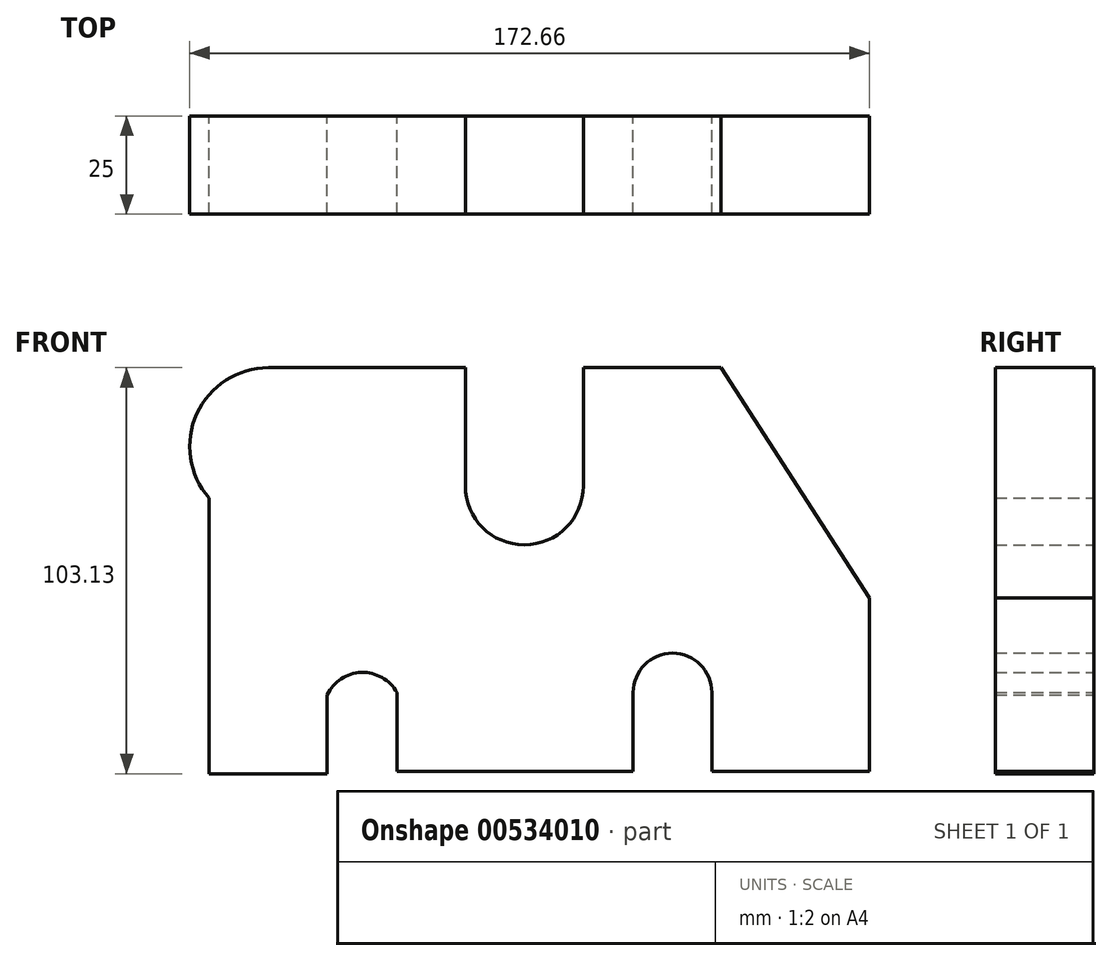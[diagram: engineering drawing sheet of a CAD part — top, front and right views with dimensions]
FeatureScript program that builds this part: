
annotation { "Feature Type Name" : "Feature", "Feature Type Description" : "" }
export const myFeature = defineFeature(function(context is Context, id is Id, definition is map)
    precondition{}
    {
        {
            var Q0;
            Q0=qCreatedBy(makeId("Front.planeOp"),FACE);
            var sketch = newSketch(context, id + "F0", { "sketchPlane" : qUnion([Q0])});
            skLineSegment(sketch, "E0", {"start": v(-105.28, 82.52) * mm, "end": v(-55.28, 82.52) * mm});
            skLineSegment(sketch, "E1", {"start": v(-55.28, 82.52) * mm, "end": v(-55.28, 52.52) * mm});
            skLineSegment(sketch, "E2", {"start": v(-25.28, 82.52) * mm, "end": v(-25.28, 52.52) * mm});
            skLineSegment(sketch, "E3", {"start": v(-25.28, 82.52) * mm, "end": v(9.72, 82.52) * mm});
            skLineSegment(sketch, "E4", {"start": v(9.72, 82.52) * mm, "end": v(47.38, 24) * mm});
            skLineSegment(sketch, "E5", {"start": v(38.76, -30.8) * mm, "end": v(37.94, -30.8) * mm});
            skLineSegment(sketch, "E6", {"start": v(-120.37, 49.39) * mm, "end": v(-120.37, -20.61) * mm});
            skLineSegment(sketch, "E7", {"start": v(-120.37, -20.61) * mm, "end": v(-90.37, -20.61) * mm});
            skArc(sketch, "E8", {"start": v(-55.28, 52.52) * mm, "mid": v(-40.28, 37.52) * mm, "end": v(-25.28, 52.52) * mm});
            skLineSegment(sketch, "E9", {"start": v(-72.62, -20) * mm, "end": v(-12.62, -20) * mm});
            skLineSegment(sketch, "E10", {"start": v(-12.62, -20) * mm, "end": v(-12.62, 0) * mm});
            skLineSegment(sketch, "E11", {"start": v(7.38, -20) * mm, "end": v(7.38, 0) * mm});
            skLineSegment(sketch, "E12", {"start": v(7.38, -20) * mm, "end": v(47.38, -20) * mm});
            skLineSegment(sketch, "E13", {"start": v(47.38, 24) * mm, "end": v(47.38, -20) * mm});
            skArc(sketch, "E14", {"start": v(7.38, 0) * mm, "mid": v(-2.62, 10) * mm, "end": v(-12.62, 0) * mm});
            skLineSegment(sketch, "E15", {"start": v(-90.37, -20.61) * mm, "end": v(-90.37, -0.61) * mm});
            skLineSegment(sketch, "E16", {"start": v(-72.62, -20) * mm, "end": v(-72.62, 0) * mm});
            skArc(sketch, "E17", {"start": v(-72.62, 0) * mm, "mid": v(-81.68, 5.1) * mm, "end": v(-90.37, -0.61) * mm});
            skArc(sketch, "E18", {"start": v(-105.28, 82.52) * mm, "mid": v(-123.48, 70.8) * mm, "end": v(-120.37, 49.39) * mm});
            skSolve(sketch);
        }
        {
            var Q0;
            Q0 = qSketchRegion(id + "F0", true);
            extrude(context, id + "F1", {"entities" : qUnion([Q0]), "depth" : 25 * mm, "offsetDistance" : 25 * mm});
        }
    });
